# Revit family: ThinkingWall Acoustic AV
name_source: partatom
category: Generic Models
units: mm (PartAtom-declared; Revit-internal decimal feet)

## family parameters
Always vertical = Yes
Can host rebar = No
Cut with Voids When Loaded = No
Maintain Annotation Orientation = No
Part Type = Normal
Room Calculation Point = No
Round Connector Dimension = Use Diameter
Shared = No
Work Plane-Based = No

## types (6) — shared parameters
Acoustic Colour = <By Category>
Description = Mobile freestanding acoustic AV unit. Part of the ThinkingWall® range for flexible breakout and meeting spaces.
Manufacturer = Logovisual LTD
Model = ThinkingWall® Acoustic AV
Plinth Colour = <By Category>
Plug = Yes
Steel Colour = <By Category>
URL = https://www.logovisual.com
zero-valued in all types: Default Elevation

## per-type parameters (varying)
| type | Length | No of Slat | Panel | TV Height | TV Width | Whiteboard |
| ThinkingWall® Acoustic AV 1200 Whiteboard to other side | 1200 mm | 29 | No | 565 mm | 965 mm | Yes |
| ThinkingWall® Acoustic AV 1500 Whiteboard to other side | 1500 mm | 36 | No | 720 mm  [stored 2.3622 ft] | 1230 mm  [stored 4.03543 ft] | Yes |
| ThinkingWall® Acoustic AV 1800 Whiteboard to other side | 1800 mm  [stored 5.90551 ft] | 43 | No | 830 mm  [stored 2.7231 ft] | 1450 mm  [stored 4.75722 ft] | Yes |
| ThinkingWall® Acoustic AV 1200 Acoustic to both sides | 1200 mm | 29 | Yes | 565 mm | 965 mm | No |
| ThinkingWall® Acoustic AV 1500 Acoustic to both sides | 1500 mm | 36 | Yes | 720 mm  [stored 2.3622 ft] | 1230 mm  [stored 4.03543 ft] | No |
| ThinkingWall® Acoustic AV 1800 Acoustic to both sides | 1800 mm  [stored 5.90551 ft] | 43 | Yes | 830 mm  [stored 2.7231 ft] | 1450 mm  [stored 4.75722 ft] | No |

note: [stored X ft] marks values corroborated as IEEE doubles in the binary element streams (Revit-internal decimal feet)

## geometry (parser evidence)
native form markers: Sweep x25
no freeform markers — native parametric forms only
